# Revit family: HeatPump_WaterToWater_Rheem_16kW_LowGWP
name_source: partatom
category: Mechanical Equipment
units: mm (PartAtom-declared; Revit-internal decimal feet)

## family parameters
Always vertical = Yes
Classification = None
Cut with Voids When Loaded = No
OmniClass Number = 23.33.17.00
OmniClass Title = Heat Pumps
Part Type = Normal
Room Calculation Point = No
Round Connector Dimension = Use Diameter
Shared = No
Work Plane-Based = No

## types (1)
- 95501600
    ApparentLoad = 18 VA
    Assembly Code = D3020
    BodyMaterial = Aluminium_PowderCoat_Rheem_White
    Default Elevation = 0 mm  [stored 0 ft]
    Description = Rheem’s YF Series Commercial heat pump uses 1234yf refrigerant which has an ultra-low Global Warming Potential (GWP) of <1. Delivering hot water up to 65°C and designed to operate in condenser loop systems with a shell and tube heat exchanger to resist fouling whilst producing a Coefficient of Performance (COP) of up to 7 in condenser loops operating at 35°C. All models are designed to be stacked to save space and available with double wall brazed plate stainless steel heat exchangers or  vented copper tube in tube heat exchangers better suited to challenging water chemistries.
    IfcExportAs = IfcPump
    IfcExportType = USERDEFINED
    Manufacturer = Rheem
    ManufacturerOverallDepth = 605 mm  [stored 1.98491 ft]
    ManufacturerOverallHeight = 972 mm
    ManufacturerOverallWidth = 1051 mm
    ManufacturerSpecCode = 95501600
    ManufacturerURLProductSpecific = https://www.rheem.com.au
    Model = 95501600
    ModifiedIssue = 20240801 $
    PowerFactor = 1
    Type Comments = HeatPump - WaterToWater - 16kW - LowGWP
    URL = https://www.rheem.com.au
    Uniclass2015Code = Pr_70_60_37_98
    Uniclass2015Title = Water to water heat pumps
    Uniclass2015Version = v1.33
    Voltage = 230 V

note: [stored X ft] marks values corroborated as IEEE doubles in the binary element streams (Revit-internal decimal feet)

## geometry (parser evidence)
native form markers: Sweep x3
no freeform markers — native parametric forms only
